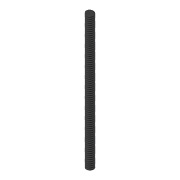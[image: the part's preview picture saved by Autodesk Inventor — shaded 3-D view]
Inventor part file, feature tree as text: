
AUTODESK INVENTOR PART (.ipt)
format: ipt  version: 2020 (Build 240168000, 168)  size: 2,642,944 bytes
history: native  units: mm
features: extrude x1, sketch x1, other x1
ambient origin geometry x8: Origin, YZ Plane, XZ Plane, XY Plane, X Axis, Y Axis, Z Axis, Center Point
bodies: Solid1 (feature_tree)
feature tree (3):
  extrude  "Extrusion1"  [1 undecoded]
  sketch  "Sketch1"  dims[d0=200.0mm d1=0.0mm]
  other  "Cut-Sweep1"
note: 1 required parameter value undecoded (feature->parameter linkage not recoverable at this tier; creation-order binding heuristic only, values carry confidence <= 0.55)
